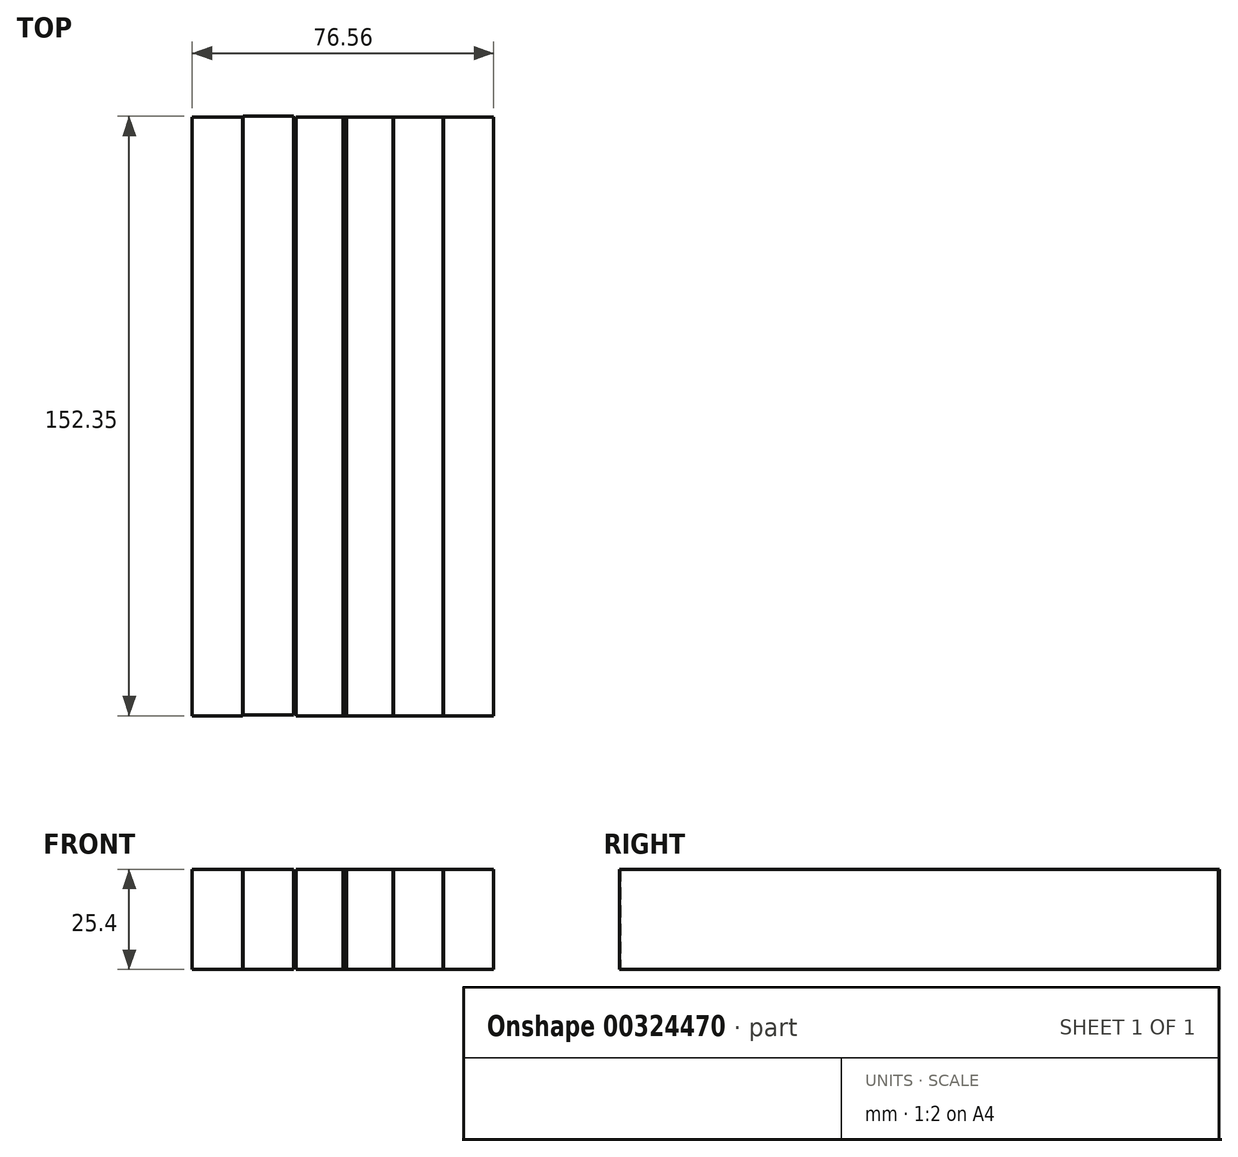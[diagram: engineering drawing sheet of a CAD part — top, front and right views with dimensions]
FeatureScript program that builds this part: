
annotation { "Feature Type Name" : "Feature", "Feature Type Description" : "" }
export const myFeature = defineFeature(function(context is Context, id is Id, definition is map)
    precondition{}
    {
        {
            var Q0;
            Q0=qCreatedBy(makeId("Top.planeOp"),FACE);
            var sketch = newSketch(context, id + "F0", { "sketchPlane" : qUnion([Q0])});
            skLineSegment(sketch, "E0.bottom", {"start": v(-75.29, 76.05) * mm, "end": v(-62.48, 76.05) * mm});
            skLineSegment(sketch, "E0.top", {"start": v(-75.29, -76.05) * mm, "end": v(-62.48, -76.05) * mm});
            skLineSegment(sketch, "E0.left", {"start": v(-75.29, 76.05) * mm, "end": v(-75.29, -76.05) * mm});
            skLineSegment(sketch, "E0.right", {"start": v(-62.48, 76.05) * mm, "end": v(-62.48, -76.05) * mm});
            skSolve(sketch);
        }
        {
            var Q0;
            Q0 = qSketchRegion(id + "F0", true);
            extrude(context, id + "F1", {"entities" : qUnion([Q0]), "depth" : 25.4 * mm});
        }
        {
            var Q0;
            Q0=makeQuery(id+"F1.opExtrude","SWEPT_BODY",BODY,{"disambiguationData":[OSD([sQuery(id+"F0.wireOp",EDGE,"E0.bottom"),sQuery(id+"F0.wireOp",EDGE,"E0.top"),sQuery(id+"F0.wireOp",EDGE,"E0.left"),sQuery(id+"F0.wireOp",EDGE,"E0.right")])]});
            transform(context, id + "F2", {"entities" : qUnion([Q0]), "transformType" : TransformType.TRANSLATION_3D, "dx" : 12.95 * mm, "dy" : 0.25 * mm, "dz" : 0 * mm, "makeCopy" : true});
        }
        {
            var Q0;
            Q0=makeQuery(id+"F2.opPattern","COPY",BODY,{"derivedFrom":makeQuery(id+"F1.opExtrude","SWEPT_BODY",BODY,{"disambiguationData":[OSD([sQuery(id+"F0.wireOp",EDGE,"E0.bottom"),sQuery(id+"F0.wireOp",EDGE,"E0.top"),sQuery(id+"F0.wireOp",EDGE,"E0.left"),sQuery(id+"F0.wireOp",EDGE,"E0.right")])]}),"instanceName":"1"});
            transform(context, id + "F3", {"entities" : qUnion([Q0]), "transformType" : TransformType.TRANSLATION_3D, "dx" : 13.46 * mm, "dy" : -0.25 * mm, "dz" : 0 * mm, "makeCopy" : true});
        }
        {
            var Q0;
            Q0=makeQuery(id+"F2.opPattern","COPY",BODY,{"derivedFrom":makeQuery(id+"F1.opExtrude","SWEPT_BODY",BODY,{"disambiguationData":[OSD([sQuery(id+"F0.wireOp",EDGE,"E0.bottom"),sQuery(id+"F0.wireOp",EDGE,"E0.top"),sQuery(id+"F0.wireOp",EDGE,"E0.left"),sQuery(id+"F0.wireOp",EDGE,"E0.right")])]}),"instanceName":"1"});
            transform(context, id + "F4", {"entities" : qUnion([Q0]), "transformType" : TransformType.TRANSLATION_3D, "dx" : 13.72 * mm, "dy" : 0 * mm, "dz" : 0 * mm, "makeCopy" : true});
        }
        {
            var Q0;
            Q0=makeQuery(id+"F4.opPattern","COPY",BODY,{"derivedFrom":makeQuery(id+"F2.opPattern","COPY",BODY,{"derivedFrom":makeQuery(id+"F1.opExtrude","SWEPT_BODY",BODY,{"disambiguationData":[OSD([sQuery(id+"F0.wireOp",EDGE,"E0.bottom"),sQuery(id+"F0.wireOp",EDGE,"E0.top"),sQuery(id+"F0.wireOp",EDGE,"E0.left"),sQuery(id+"F0.wireOp",EDGE,"E0.right")])]}),"instanceName":"1"}),"instanceName":"1"});
            deleteBodies(context, id + "F5", {"entities" : qUnion([Q0])});
        }
        {
            var Q0;
            Q0=makeQuery(id+"F3.opPattern","COPY",BODY,{"derivedFrom":makeQuery(id+"F2.opPattern","COPY",BODY,{"derivedFrom":makeQuery(id+"F1.opExtrude","SWEPT_BODY",BODY,{"disambiguationData":[OSD([sQuery(id+"F0.wireOp",EDGE,"E0.bottom"),sQuery(id+"F0.wireOp",EDGE,"E0.top"),sQuery(id+"F0.wireOp",EDGE,"E0.left"),sQuery(id+"F0.wireOp",EDGE,"E0.right")])]}),"instanceName":"1"}),"instanceName":"1"});
            transform(context, id + "F6", {"entities" : qUnion([Q0]), "transformType" : TransformType.TRANSLATION_3D, "dx" : 11.94 * mm, "dy" : 0 * mm, "dz" : 0 * mm, "makeCopy" : true});
        }
        {
            var Q0;
            Q0=makeQuery(id+"F6.opPattern","COPY",BODY,{"derivedFrom":makeQuery(id+"F3.opPattern","COPY",BODY,{"derivedFrom":makeQuery(id+"F2.opPattern","COPY",BODY,{"derivedFrom":makeQuery(id+"F1.opExtrude","SWEPT_BODY",BODY,{"disambiguationData":[OSD([sQuery(id+"F0.wireOp",EDGE,"E0.bottom"),sQuery(id+"F0.wireOp",EDGE,"E0.top"),sQuery(id+"F0.wireOp",EDGE,"E0.left"),sQuery(id+"F0.wireOp",EDGE,"E0.right")])]}),"instanceName":"1"}),"instanceName":"1"}),"instanceName":"1"});
            transform(context, id + "F7", {"entities" : qUnion([Q0]), "transformType" : TransformType.TRANSLATION_3D, "dx" : 12.7 * mm, "dy" : 0 * mm, "dz" : 0 * mm, "makeCopy" : true});
        }
        {
            var Q0;
            Q0=makeQuery(id+"F7.opPattern","COPY",BODY,{"derivedFrom":makeQuery(id+"F6.opPattern","COPY",BODY,{"derivedFrom":makeQuery(id+"F3.opPattern","COPY",BODY,{"derivedFrom":makeQuery(id+"F2.opPattern","COPY",BODY,{"derivedFrom":makeQuery(id+"F1.opExtrude","SWEPT_BODY",BODY,{"disambiguationData":[OSD([sQuery(id+"F0.wireOp",EDGE,"E0.bottom"),sQuery(id+"F0.wireOp",EDGE,"E0.top"),sQuery(id+"F0.wireOp",EDGE,"E0.left"),sQuery(id+"F0.wireOp",EDGE,"E0.right")])]}),"instanceName":"1"}),"instanceName":"1"}),"instanceName":"1"}),"instanceName":"1"});
            transform(context, id + "F8", {"entities" : qUnion([Q0]), "transformType" : TransformType.TRANSLATION_3D, "dx" : 12.7 * mm, "dy" : 0 * mm, "dz" : 0 * mm, "makeCopy" : true});
        }
    });
